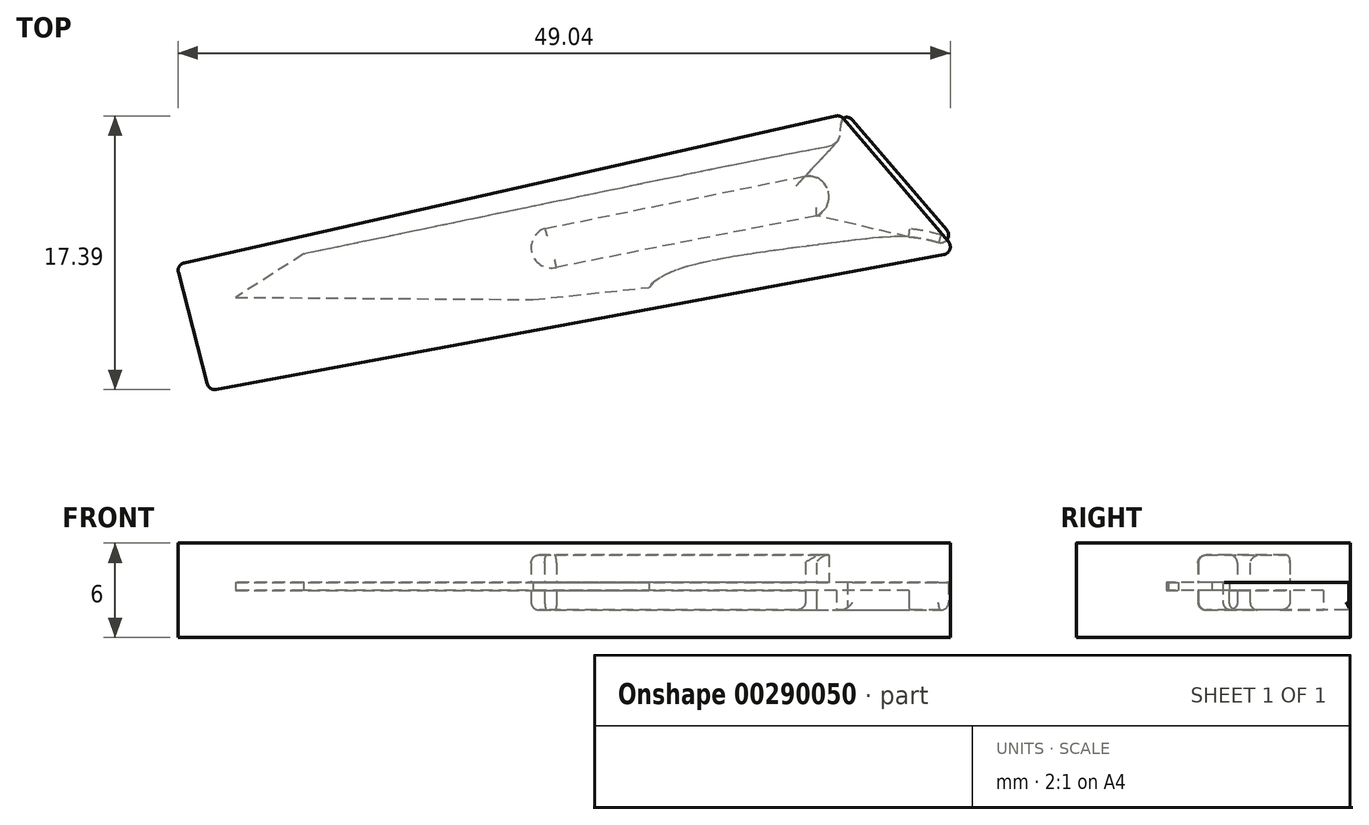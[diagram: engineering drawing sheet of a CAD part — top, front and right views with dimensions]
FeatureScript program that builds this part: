
annotation { "Feature Type Name" : "Feature", "Feature Type Description" : "" }
export const myFeature = defineFeature(function(context is Context, id is Id, definition is map)
    precondition{}
    {
        {
            var Q0;
            Q0=qCreatedBy(makeId("Top.planeOp"),FACE);
            var sketch = newSketch(context, id + "F0", { "sketchPlane" : qUnion([Q0])});
            skFitSpline(sketch, "E0", {"points": [v(39.35, -5.53) * mm, v(37.84, -5.18) * mm, v(35.74, -4.72) * mm, v(29.9, -5.2) * mm, v(20.66, -6.84) * mm, v(19, -7.92) * mm], "startDerivative": vector(-9.45, 1.89) * mm, "endDerivative": vector(-5.02, -6.74) * mm});
            skLineSegment(sketch, "E1", {"start": v(-2.94, -5.8) * mm, "end": v(-7.23, -8.54) * mm});
            skLineSegment(sketch, "E2", {"start": v(-7.23, -8.54) * mm, "end": v(11.66, -8.69) * mm});
            skLineSegment(sketch, "E3", {"start": v(11.66, -8.69) * mm, "end": v(19, -7.92) * mm});
            skLineSegment(sketch, "E4", {"start": v(31.95, 2.7) * mm, "end": v(38.94, -5.44) * mm});
            skPoint(sketch, "E5", {"position": v(31.95, 2.7) * mm});
            skPoint(sketch, "E6", {"position": v(31.6, 2.9) * mm});
            skFitSpline(sketch, "E7.trimOffspring", {"points": [v(32.13, 2.82) * mm, v(31.3, 2.77) * mm, v(31.06, 1.5) * mm, v(29.4, 0.82) * mm, v(-2.94, -5.8) * mm], "startDerivative": vector(-9.88, 2.18) * mm, "endDerivative": vector(-66.22, -13.7) * mm});
            skArc(sketch, "E8", {"start": v(31.95, 2.7) * mm, "mid": v(31.8, 2.83) * mm, "end": v(31.6, 2.9) * mm});
            skSolve(sketch);
        }
        {
            var Q0;
            Q0 = qSketchRegion(id + "F0", true);
            extrude(context, id + "F1", {"entities" : qUnion([Q0]), "depth" : 0.5 * mm});
        }
        {
            var Q0;
            Q0=makeQuery(id+"F1.opExtrude","CAP_FACE",FACE,{"disambiguationData":[OSD([sQuery(id+"F0.wireOp",EDGE,"ebd00a47-fdcf-4052-8c77-980814e3eb3e"),sQuery(id+"F0.wireOp",EDGE,"E0"),sQuery(id+"F0.wireOp",EDGE,"E1"),sQuery(id+"F0.wireOp",EDGE,"E2"),sQuery(id+"F0.wireOp",EDGE,"E3"),sQuery(id+"F0.wireOp",EDGE,"E4")])],"isStart":false});
            var sketch = newSketch(context, id + "F2", { "sketchPlane" : qUnion([Q0])});
            skArc(sketch, "E9", {"start": v(12.4, -4.17) * mm, "mid": v(11.59, -5.76) * mm, "end": v(13.14, -6.64) * mm});
            skArc(sketch, "E10", {"start": v(29.64, -3.37) * mm, "mid": v(30.4, -1.8) * mm, "end": v(28.94, -0.84) * mm});
            skLineSegment(sketch, "E11", {"start": v(28.94, -0.84) * mm, "end": v(12.4, -4.17) * mm});
            skLineSegment(sketch, "E12", {"start": v(13.14, -6.64) * mm, "end": v(29.64, -3.37) * mm});
            skSolve(sketch);
        }
        {
            var Q0;
            Q0=makeQuery(id+"F2.imprint","IMPRINT",FACE,{"disambiguationData":[TD([[makeQuery(id+"F2.imprint","IMPRINT",EDGE,{"derivedFrom":sQuery(id+"F2.wireOp",EDGE,"E9")}),1.0]])]});
            extrude(context, id + "F3", {"entities" : qUnion([Q0]), "operationType" : NewBodyOperationType.ADD, "endBound" : BoundingType.SYMMETRIC, "depth" : 3.5 * mm});
        }
        {
            var Q0;
            Q0=makeQuery(id+"F1.opExtrude","CAP_FACE",FACE,{"disambiguationData":[OSD([sQuery(id+"F0.wireOp",EDGE,"ebd00a47-fdcf-4052-8c77-980814e3eb3e"),sQuery(id+"F0.wireOp",EDGE,"E0"),sQuery(id+"F0.wireOp",EDGE,"E1"),sQuery(id+"F0.wireOp",EDGE,"E2"),sQuery(id+"F0.wireOp",EDGE,"E3"),sQuery(id+"F0.wireOp",EDGE,"E4")])],"isStart":false});
            var sketch = newSketch(context, id + "F4", { "sketchPlane" : qUnion([Q0])});
            skLineSegment(sketch, "E13.0.0", {"start": v(13.14, -6.64) * mm, "end": v(29.64, -3.37) * mm});
            skArc(sketch, "E13.0.1", {"start": v(29.64, -3.37) * mm, "mid": v(30.4, -1.8) * mm, "end": v(28.94, -0.84) * mm});
            skLineSegment(sketch, "E13.0.2", {"start": v(28.94, -0.84) * mm, "end": v(12.4, -4.17) * mm});
            skArc(sketch, "E13.0.3", {"start": v(12.4, -4.17) * mm, "mid": v(11.59, -5.76) * mm, "end": v(13.14, -6.64) * mm});
            skLineSegment(sketch, "E14", {"start": v(29.64, -3.37) * mm, "end": v(35.51, -4.7) * mm});
            skLineSegment(sketch, "E15", {"start": v(28.94, -0.84) * mm, "end": v(30.91, 1.27) * mm});
            skSolve(sketch);
        }
        {
            var Q0;
            Q0=makeQuery(id+"F4.imprint","IMPRINT",FACE,{"disambiguationData":[TD([[makeQuery(id+"F4.imprint","IMPRINT",EDGE,{"derivedFrom":sQuery(id+"F4.wireOp",EDGE,"E13.0.1")}),1.0]])]});
            extrude(context, id + "F5", {"entities" : qUnion([Q0]), "operationType" : NewBodyOperationType.ADD, "endBound" : BoundingType.SYMMETRIC, "depth" : 3.5 * mm});
        }
        {
            var Q0;
            Q0=makeQuery(id+"F4.imprint","IMPRINT",FACE,{"disambiguationData":[TD([[makeQuery(id+"F4.imprint","IMPRINT",EDGE,{"derivedFrom":sQuery(id+"F4.wireOp",EDGE,"E13.0.1")}),1.0]])]});
            extrude(context, id + "F6", {"entities" : qUnion([Q0]), "operationType" : NewBodyOperationType.REMOVE, "depth" : 1.75 * mm});
        }
        {
            var Q0;
            Q0=makeQuery(id+"F3.opExtrude","CAP_EDGE",EDGE,{"disambiguationData":[OSD([sQuery(id+"F2.wireOp",EDGE,"E11")])],"isStart":true});
            var Q1;
            Q1=makeQuery(id+"F5.opExtrude","CAP_EDGE",EDGE,{"disambiguationData":[OSD([sQuery(id+"F4.wireOp",EDGE,"E14")])],"isStart":true});
            var Q2;
            Q2=makeQuery(id+"F5.opExtrude","CAP_EDGE",EDGE,{"disambiguationData":[OSD([sQuery(id+"F0.wireOp",EDGE,"E0")])],"isStart":true});
            var Q3;
            Q3=makeQuery(id+"F3.opExtrude","CAP_EDGE",EDGE,{"disambiguationData":[OSD([sQuery(id+"F2.wireOp",EDGE,"E12")])],"isStart":true});
            var Q4;
            Q4=makeQuery(id+"F3.opExtrude","CAP_EDGE",EDGE,{"disambiguationData":[OSD([sQuery(id+"F2.wireOp",EDGE,"E9")])],"isStart":true});
            var Q5;
            Q5=makeQuery(id+"F3.opExtrude","CAP_EDGE",EDGE,{"disambiguationData":[OSD([sQuery(id+"F2.wireOp",EDGE,"E11")])],"isStart":false});
            var Q6;
            Q6=makeQuery(id+"F3.opExtrude","CAP_EDGE",EDGE,{"disambiguationData":[OSD([sQuery(id+"F2.wireOp",EDGE,"E9")])],"isStart":false});
            var Q7;
            Q7=makeQuery(id+"F6.boolean.opBoolean","COPY",EDGE,{"derivedFrom":makeQuery(id+"F6.opExtrude","CAP_EDGE",EDGE,{"disambiguationData":[OSD([sQuery(id+"F4.wireOp",EDGE,"E13.0.1")])],"isStart":false})});
            fillet(context, id + "F7", {"entities" : qUnion([Q0, Q1, Q2, Q3, Q4, Q5, Q6, Q7]), "radius" : 0.5 * mm, "tangentPropagation" : true, "allowEdgeOverflow" : false});
        }
        {
            var Q0;
            Q0=makeQuery(id+"F5.opExtrude","CAP_EDGE",EDGE,{"disambiguationData":[OSD([sQuery(id+"F0.wireOp",EDGE,"E4")])],"isStart":true});
            fillet(context, id + "F8", {"entities" : qUnion([Q0]), "radius" : 0.5 * mm, "tangentPropagation" : true, "allowEdgeOverflow" : false});
        }
        {
            var Q0;
            Q0=qCreatedBy(makeId("Top.planeOp"),FACE);
            var sketch = newSketch(context, id + "F9", { "sketchPlane" : qUnion([Q0])});
            skLineSegment(sketch, "E16", {"start": v(30.87, 2.97) * mm, "end": v(-10.5, -6.35) * mm});
            skLineSegment(sketch, "E17", {"start": v(37.74, -5.83) * mm, "end": v(-8.47, -14.4) * mm});
            skLineSegment(sketch, "E18", {"start": v(-9.04, -14.03) * mm, "end": v(-10.88, -6.96) * mm});
            skLineSegment(sketch, "E19", {"start": v(31.36, 2.8) * mm, "end": v(38.03, -5.01) * mm});
            skPoint(sketch, "E20.visualSharp", {"position": v(-11, -6.46) * mm});
            skArc(sketch, "E20.filletArc", {"start": v(-10.5, -6.35) * mm, "mid": v(-10.82, -6.58) * mm, "end": v(-10.88, -6.96) * mm});
            skPoint(sketch, "E21.visualSharp", {"position": v(-8.93, -14.48) * mm});
            skArc(sketch, "E21.filletArc", {"start": v(-9.04, -14.03) * mm, "mid": v(-8.83, -14.33) * mm, "end": v(-8.47, -14.4) * mm});
            skPoint(sketch, "E22.visualSharp", {"position": v(38.6, -5.67) * mm});
            skArc(sketch, "E22.filletArc", {"start": v(37.74, -5.83) * mm, "mid": v(38.12, -5.5) * mm, "end": v(38.03, -5.01) * mm});
            skPoint(sketch, "E23.visualSharp", {"position": v(31.17, 3.04) * mm});
            skArc(sketch, "E23.filletArc", {"start": v(31.36, 2.8) * mm, "mid": v(31.14, 2.96) * mm, "end": v(30.87, 2.97) * mm});
            skSolve(sketch);
        }
        {
            var Q0;
            Q0=makeQuery(id+"F9.imprint","IMPRINT",FACE,{"disambiguationData":[TD([[makeQuery(id+"F9.imprint","IMPRINT",EDGE,{"derivedFrom":sQuery(id+"F9.wireOp",EDGE,"E16")}),1.0]])]});
            extrude(context, id + "F10", {"entities" : qUnion([Q0]), "endBound" : BoundingType.SYMMETRIC, "depth" : 6 * mm});
        }
    });
